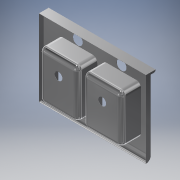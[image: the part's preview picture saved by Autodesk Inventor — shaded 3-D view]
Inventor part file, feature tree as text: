
AUTODESK INVENTOR PART (.ipt)
format: ipt  version: 2016 (Build 200138000, 138)  size: 327,168 bytes
history: native  units: mm
features: sketch x4, extrude x4, fillet x2, shell x2, other x1, projected_geometry x1
ambient origin geometry x8: Origin, YZ Plane, XZ Plane, XY Plane, X Axis, Y Axis, Z Axis, Center Point
bodies: Body1 (feature_tree)
feature tree (14):
  other  "Sólido1"
  sketch  "Boceto1"  dims[d2=400.0mm d3=500.0mm d4=2.0mm d5=50.0mm]
  extrude  "Extrusión1"  Depth=500.0mm
  sketch  "Boceto15"  dims[d10=200.0mm d11=0.0mm d41=850.0mm]
  fillet  "Fillet2"  Radius=2.0mm
  shell  "Shell2"  Thickness=50.0mm
  extrude  "Extrusion13"  Depth=850.0mm
  extrude  "Extrusion14"  Depth=50.0mm
  sketch  "Sketch25"  dims[d84=400.0mm d85=500.0mm d86=50.0mm d88=1.2mm d89=50.0mm d90=1.0mm d91=50.0mm d92=0.0mm d93=20.0mm d94=100.0mm d95=20.0mm d96=1100.0mm d97=0.0mm d100=450.0mm d101=25.0mm d102=55.0mm d103=100.0mm d104=100.0mm d105=225.0mm d106=225.0mm d107=80.0mm d108=80.0mm d109=50.0mm d110=1.0mm d111=0.0mm d112=0.0mm]
  fillet  "Fillet3"  Radius=100.0mm
  shell  "Shell3"  Thickness=50.0mm
  extrude  "Extrusion15"  Depth=500.0mm
  projected_geometry  "Projected Loop1"
  sketch  "Sketch24"  dims[d42=500.0mm d43=50.0mm d81=100.0mm d83=50.0mm]
